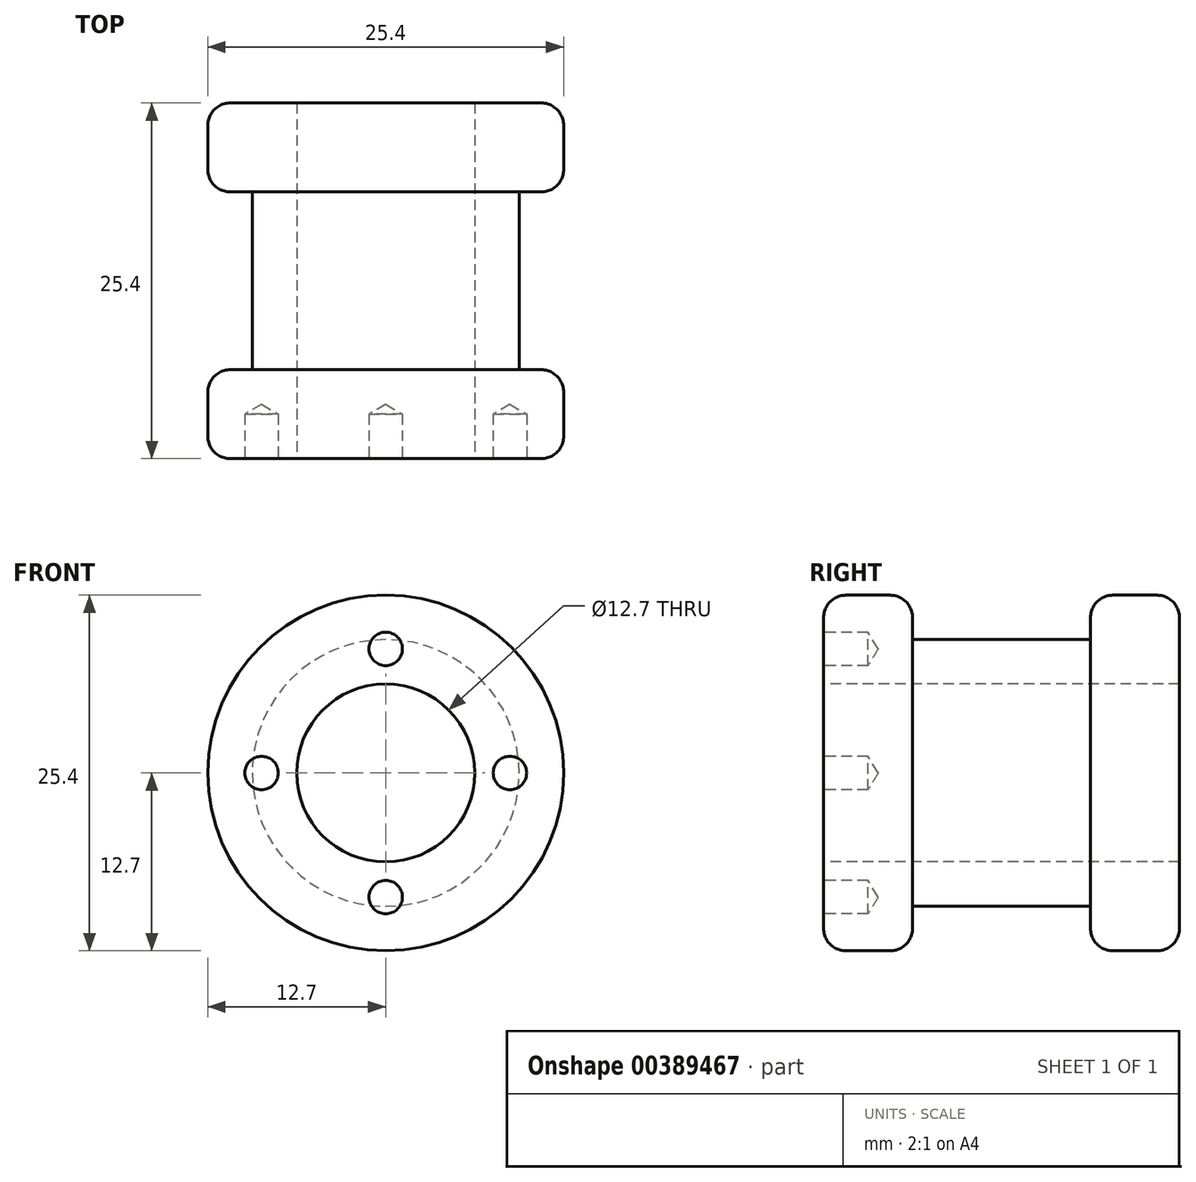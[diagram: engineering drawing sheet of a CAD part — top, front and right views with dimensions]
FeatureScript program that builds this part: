
annotation { "Feature Type Name" : "Feature", "Feature Type Description" : "" }
export const myFeature = defineFeature(function(context is Context, id is Id, definition is map)
    precondition{}
    {
        {
            var Q0;
            Q0=qCreatedBy(makeId("Front.planeOp"),FACE);
            var sketch = newSketch(context, id + "F0", { "sketchPlane" : qUnion([Q0])});
            skCircle(sketch, "E0", {"center": v(0, 0) * mm, "radius": 12.7 * mm});
            skSolve(sketch);
        }
        {
            var Q0;
            Q0 = qSketchRegion(id + "F0", true);
            extrude(context, id + "F1", {"entities" : qUnion([Q0]), "depth" : 6.35 * mm});
        }
        {
            var Q0;
            Q0=makeQuery(id+"F1.opExtrude","CAP_FACE",FACE,{"disambiguationData":[OSD([sQuery(id+"F0.wireOp",EDGE,"E0")])],"isStart":true});
            var sketch = newSketch(context, id + "F2", { "sketchPlane" : qUnion([Q0])});
            skCircle(sketch, "E1", {"center": v(0, 0) * mm, "radius": 9.53 * mm});
            skSolve(sketch);
        }
        {
            var Q0;
            Q0 = qSketchRegion(id + "F2", true);
            extrude(context, id + "F3", {"entities" : qUnion([Q0]), "operationType" : NewBodyOperationType.ADD, "depth" : 12.7 * mm});
        }
        {
            var Q0;
            Q0=makeQuery(id+"F3.opExtrude","CAP_FACE",FACE,{"disambiguationData":[OSD([sQuery(id+"F2.wireOp",EDGE,"E1")])],"isStart":false});
            var sketch = newSketch(context, id + "F4", { "sketchPlane" : qUnion([Q0])});
            skCircle(sketch, "E2", {"center": v(0, 0) * mm, "radius": 12.7 * mm});
            skSolve(sketch);
        }
        {
            var Q0;
            Q0 = qSketchRegion(id + "F4", true);
            extrude(context, id + "F5", {"entities" : qUnion([Q0]), "operationType" : NewBodyOperationType.ADD, "depth" : 6.35 * mm});
        }
        {
            var Q0;
            Q0=makeQuery(id+"F1.opExtrude","CAP_FACE",FACE,{"disambiguationData":[OSD([sQuery(id+"F0.wireOp",EDGE,"E0")])],"isStart":false});
            var Q1;
            Q1=makeQuery(id+"F5.opExtrude","CAP_FACE",FACE,{"disambiguationData":[OSD([sQuery(id+"F4.wireOp",EDGE,"E2")])],"isStart":false});
            var Q2;
            Q2=makeQuery(id+"F1.opExtrude","CAP_EDGE",EDGE,{"disambiguationData":[OSD([sQuery(id+"F0.wireOp",EDGE,"E0")])],"isStart":true});
            var Q3;
            Q3=makeQuery(id+"F5.opExtrude","CAP_EDGE",EDGE,{"disambiguationData":[OSD([sQuery(id+"F4.wireOp",EDGE,"E2")])],"isStart":true});
            fillet(context, id + "F6", {"entities" : qUnion([Q0, Q1, Q2, Q3]), "radius" : 1.6 * mm, "tangentPropagation" : true, "allowEdgeOverflow" : false});
        }
        {
            var Q0;
            Q0=makeQuery(id+"F1.opExtrude","CAP_FACE",FACE,{"disambiguationData":[OSD([sQuery(id+"F0.wireOp",EDGE,"E0")])],"isStart":false});
            var sketch = newSketch(context, id + "F7", { "sketchPlane" : qUnion([Q0])});
            skPoint(sketch, "E3", {"position": v(0, 0) * mm});
            skSolve(sketch);
        }
        {
            var Q0;
            Q0=sQuery(id+"F7.wireOp",VERTEX,"E3");
            var Q1;
            Q1=makeQuery(id+"F1.opExtrude","SWEPT_BODY",BODY,{"disambiguationData":[OSD([sQuery(id+"F0.wireOp",EDGE,"E0")])]});
            hole(context, id + "F8", {"style" : HoleStyle.SIMPLE, "endStyle" : HoleEndStyle.THROUGH, "holeDiameter" : 12.7 * mm, "isTappedThrough" : true, "tappedDepth" : 12.7 * mm, "tapClearance" : 3, "locations" : qUnion([Q0]), "scope" : qUnion([Q1])});
        }
        {
            var Q0;
            Q0=makeQuery(id+"F1.opExtrude","CAP_FACE",FACE,{"disambiguationData":[OSD([sQuery(id+"F0.wireOp",EDGE,"E0")])],"isStart":false});
            var sketch = newSketch(context, id + "F9", { "sketchPlane" : qUnion([Q0])});
            skPoint(sketch, "E4", {"position": v(0, 8.86) * mm});
            skPoint(sketch, "E5.1.0", {"position": v(-8.86, 0) * mm});
            skPoint(sketch, "E5.2.0", {"position": v(0, -8.86) * mm});
            skPoint(sketch, "E5.3.0", {"position": v(8.86, 0) * mm});
            skPoint(sketch, "E5.center", {"position": v(0, 0) * mm});
            skSolve(sketch);
        }
        {
            var Q0;
            Q0=sQuery(id+"F9.wireOp",VERTEX,"E5.1.0");
            var Q1;
            Q1=sQuery(id+"F9.wireOp",VERTEX,"E5.2.0");
            var Q2;
            Q2=sQuery(id+"F9.wireOp",VERTEX,"E5.3.0");
            var Q3;
            Q3=sQuery(id+"F9.wireOp",VERTEX,"E4");
            var Q4;
            Q4=makeQuery(id+"F1.opExtrude","SWEPT_BODY",BODY,{"disambiguationData":[OSD([sQuery(id+"F0.wireOp",EDGE,"E0")])]});
            hole(context, id + "F10", {"style" : HoleStyle.SIMPLE, "endStyle" : HoleEndStyle.BLIND, "holeDiameter" : 2.4 * mm, "holeDepth" : 3.17 * mm, "isTappedThrough" : true, "tappedDepth" : 12.7 * mm, "tapClearance" : 3, "locations" : qUnion([Q0, Q1, Q2, Q3]), "scope" : qUnion([Q4])});
        }
    });
